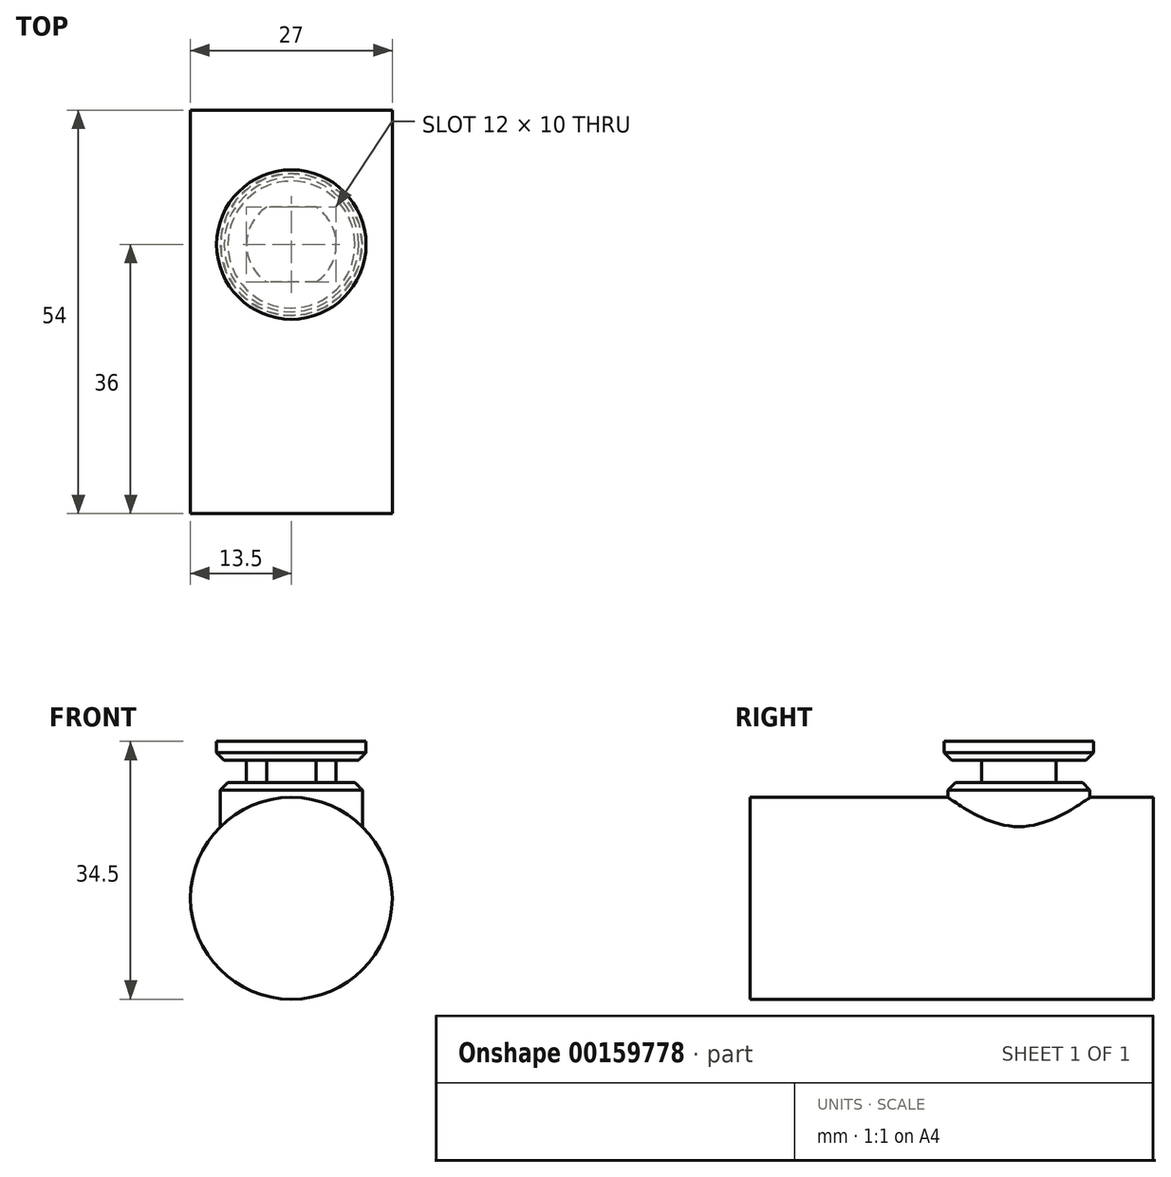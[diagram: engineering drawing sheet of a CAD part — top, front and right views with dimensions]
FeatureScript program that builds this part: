
annotation { "Feature Type Name" : "Feature", "Feature Type Description" : "" }
export const myFeature = defineFeature(function(context is Context, id is Id, definition is map)
    precondition{}
    {
        {
            var Q0;
            Q0=qCreatedBy(makeId("Front.planeOp"),FACE);
            var sketch = newSketch(context, id + "F0", { "sketchPlane" : qUnion([Q0])});
            skCircle(sketch, "E0", {"center": v(0, 0) * mm, "radius": 13.5 * mm});
            skSolve(sketch);
        }
        {
            var Q0;
            Q0 = qSketchRegion(id + "F0", true);
            extrude(context, id + "F1", {"entities" : qUnion([Q0]), "endBound" : BoundingType.SYMMETRIC, "depth" : 54 * mm});
        }
        {
            var Q0;
            Q0=qCreatedBy(makeId("Top.planeOp"),FACE);
            cPlane(context, id + "F2", {"entities" : qUnion([Q0]), "cplaneType" : CPlaneType.OFFSET, "offset" : 15.5 * mm, "width" : 150 * mm, "height" : 150 * mm});
        }
        {
            var Q0;
            Q0=qCreatedBy(id+"F2.planeOp",FACE);
            var sketch = newSketch(context, id + "F3", { "sketchPlane" : qUnion([Q0])});
            skCircle(sketch, "E1", {"center": v(0, 9) * mm, "radius": 9.5 * mm});
            skSolve(sketch);
        }
        {
            var Q0;
            Q0 = qSketchRegion(id + "F3", true);
            var Q1;
            Q1=makeQuery(id+"F1.opExtrude","SWEPT_FACE",FACE,{"disambiguationData":[OSD([sQuery(id+"F0.wireOp",EDGE,"E0")])]});
            extrude(context, id + "F4", {"entities" : qUnion([Q0]), "operationType" : NewBodyOperationType.ADD, "endBound" : BoundingType.UP_TO_SURFACE, "oppositeDirection" : true, "endBoundEntityFace" : qUnion([Q1]), "depth" : 25 * mm});
        }
        {
            var Q0;
            Q0=makeQuery(id+"F4.opExtrude","CAP_EDGE",EDGE,{"disambiguationData":[OSD([sQuery(id+"F3.wireOp",EDGE,"E1")])],"isStart":true});
            chamfer(context, id + "F5", {"entities" : qUnion([Q0]), "width" : 1 * mm, "tangentPropagation" : true});
        }
        {
            var Q0;
            Q0=makeQuery(id+"F4.opExtrude","CAP_FACE",FACE,{"disambiguationData":[OSD([sQuery(id+"F3.wireOp",EDGE,"E1")])],"isStart":true});
            var sketch = newSketch(context, id + "F6", { "sketchPlane" : qUnion([Q0])});
            skArc(sketch, "E2", {"start": v(-3.32, 14) * mm, "mid": v(-6, 9) * mm, "end": v(-3.32, 4) * mm});
            skLineSegment(sketch, "E3.bottom", {"start": v(3.32, 14) * mm, "end": v(-3.32, 14) * mm});
            skLineSegment(sketch, "E3.top", {"start": v(3.32, 4) * mm, "end": v(-3.32, 4) * mm});
            skLineSegment(sketch, "E3.left", {"start": v(3.32, 14) * mm, "end": v(3.32, 4) * mm, "construction": true});
            skLineSegment(sketch, "E3.right", {"start": v(-3.32, 14) * mm, "end": v(-3.32, 4) * mm, "construction": true});
            skArc(sketch, "E4.trimOffspring", {"start": v(3.32, 4) * mm, "mid": v(6, 9) * mm, "end": v(3.32, 14) * mm});
            skSolve(sketch);
        }
        {
            var Q0;
            Q0 = qSketchRegion(id + "F6", true);
            var Q1;
            Q1 = qConstructionFilter(qBodyType(qCreatedBy(id + "F6" ,EDGE), BodyType.WIRE), ConstructionObject.NO);
            extrude(context, id + "F7", {"entities" : qUnion([Q0]), "operationType" : NewBodyOperationType.ADD, "surfaceEntities" : qUnion([Q1]), "depth" : 3 * mm});
        }
        {
            var Q0;
            Q0=makeQuery(id+"F7.opExtrude","CAP_FACE",FACE,{"disambiguationData":[OSD([sQuery(id+"F6.wireOp",EDGE,"E2"),sQuery(id+"F6.wireOp",EDGE,"E3.bottom"),sQuery(id+"F6.wireOp",EDGE,"E3.top"),sQuery(id+"F6.wireOp",EDGE,"E4.trimOffspring")])],"isStart":false});
            var sketch = newSketch(context, id + "F8", { "sketchPlane" : qUnion([Q0])});
            skCircle(sketch, "E5", {"center": v(0, 9) * mm, "radius": 10 * mm});
            skSolve(sketch);
        }
        {
            var Q0;
            Q0 = qSketchRegion(id + "F8", true);
            extrude(context, id + "F9", {"entities" : qUnion([Q0]), "operationType" : NewBodyOperationType.ADD, "depth" : 2.5 * mm});
        }
        {
            var Q0;
            Q0=makeQuery(id+"F9.opExtrude","CAP_EDGE",EDGE,{"disambiguationData":[OSD([sQuery(id+"F8.wireOp",EDGE,"E5")])],"isStart":true});
            chamfer(context, id + "F10", {"entities" : qUnion([Q0]), "width" : 1 * mm, "tangentPropagation" : true});
        }
    });
